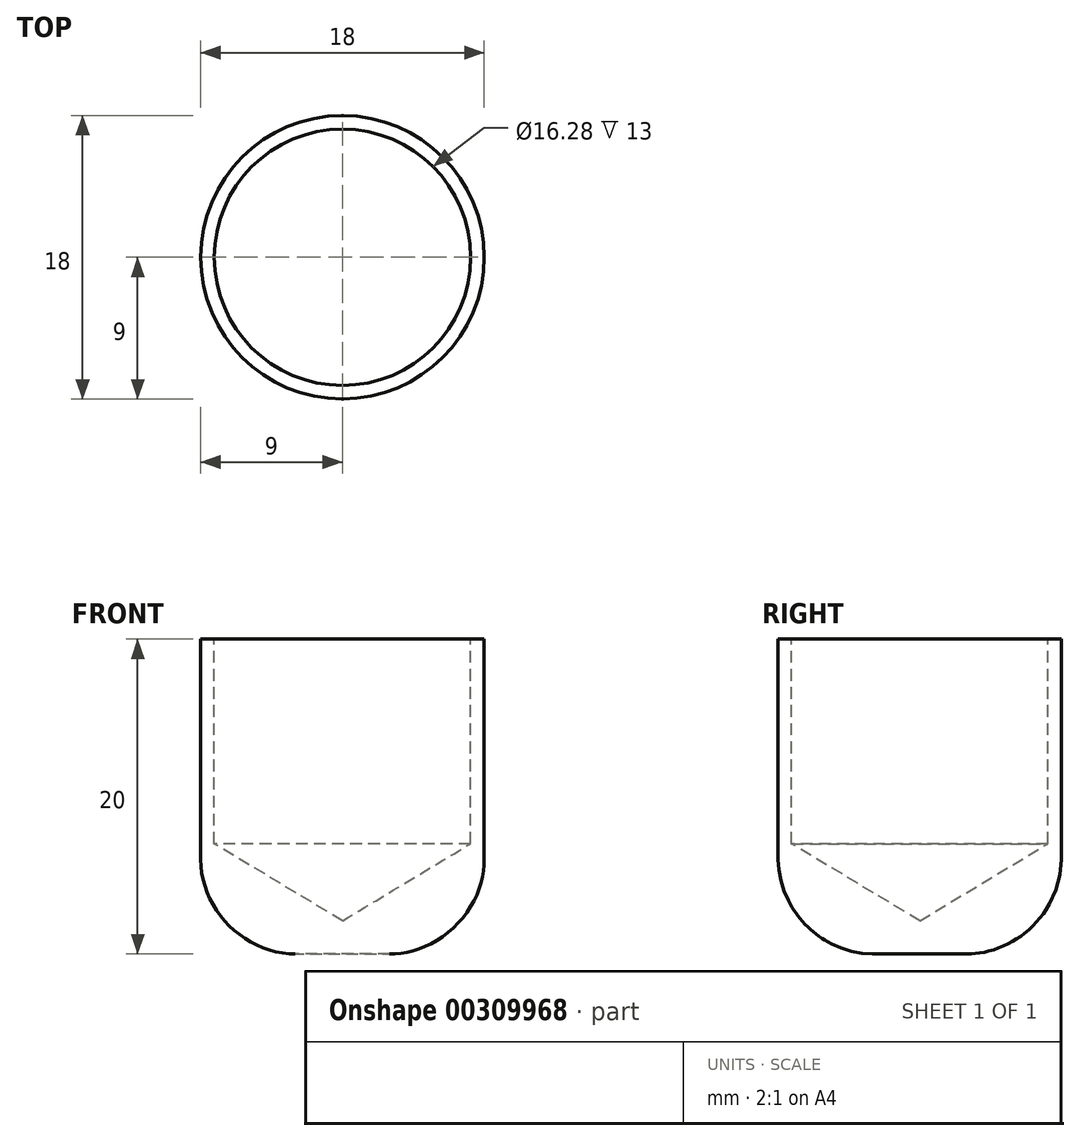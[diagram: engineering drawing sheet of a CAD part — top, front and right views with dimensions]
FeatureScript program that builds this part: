
annotation { "Feature Type Name" : "Feature", "Feature Type Description" : "" }
export const myFeature = defineFeature(function(context is Context, id is Id, definition is map)
    precondition{}
    {
        {
            var Q0;
            Q0=qCreatedBy(makeId("Top.planeOp"),FACE);
            var sketch = newSketch(context, id + "F0", { "sketchPlane" : qUnion([Q0])});
            skCircle(sketch, "E0", {"center": v(0, 0) * mm, "radius": 9 * mm});
            skSolve(sketch);
        }
        {
            var Q0;
            Q0=qCreatedBy(makeId("Top.planeOp"),FACE);
            var sketch = newSketch(context, id + "F1", { "sketchPlane" : qUnion([Q0])});
            skPoint(sketch, "E1", {"position": v(0, 0) * mm});
            skSolve(sketch);
        }
        {
            var Q0;
            Q0=makeQuery(id+"F0.imprint","IMPRINT",FACE,{"disambiguationData":[TD([[makeQuery(id+"F0.imprint","IMPRINT",EDGE,{"derivedFrom":sQuery(id+"F0.wireOp",EDGE,"E0")}),1.0]])]});
            var sketch = newSketch(context, id + "F2", { "sketchPlane" : qUnion([Q0])});
            skSolve(sketch);
        }
        {
            var Q0;
            Q0 = qSketchRegion(id + "F2", true);
            var Q1;
            Q1=makeQuery(id+"F0.imprint","IMPRINT",FACE,{"disambiguationData":[TD([[makeQuery(id+"F0.imprint","IMPRINT",EDGE,{"derivedFrom":sQuery(id+"F0.wireOp",EDGE,"E0")}),1.0]])]});
            extrude(context, id + "F3", {"entities" : qUnion([Q0, Q1]), "oppositeDirection" : true, "depth" : 20 * mm});
        }
        {
            var Q0;
            Q0=sQuery(id+"F1.wireOp",VERTEX,"E1");
            var Q1;
            Q1=makeQuery(id+"F3.opExtrude","SWEPT_BODY",BODY,{"disambiguationData":[OSD([sQuery(id+"F0.wireOp",EDGE,"E0")])]});
            hole(context, id + "F4", {"style" : HoleStyle.SIMPLE, "endStyle" : HoleEndStyle.BLIND, "standardTappedOrClearance" : lookupTablePath({ "standard" : "ANSI", "fit" : "Close", "size" : "5/8", "type" : "Clearance" }), "standardBlindInLast" : lookupTablePath({ "fit" : "Close", "standard" : "ANSI", "size" : "5/8", "type" : "Clearance" }), "holeDiameter" : 16.28 * mm, "holeDepth" : 13 * mm, "tappedDepth" : 8.82 * mm, "tapClearance" : 3, "locations" : qUnion([Q0]), "scope" : qUnion([Q1])});
        }
        {
            var Q0;
            Q0=makeQuery(id+"F3.opExtrude","CAP_EDGE",EDGE,{"disambiguationData":[OSD([sQuery(id+"F0.wireOp",EDGE,"E0")])],"isStart":false});
            fillet(context, id + "F5", {"entities" : qUnion([Q0]), "radius" : 6 * mm, "tangentPropagation" : true, "rho" : .4, "crossSection" : FilletCrossSection.CONIC, "allowEdgeOverflow" : false});
        }
    });
